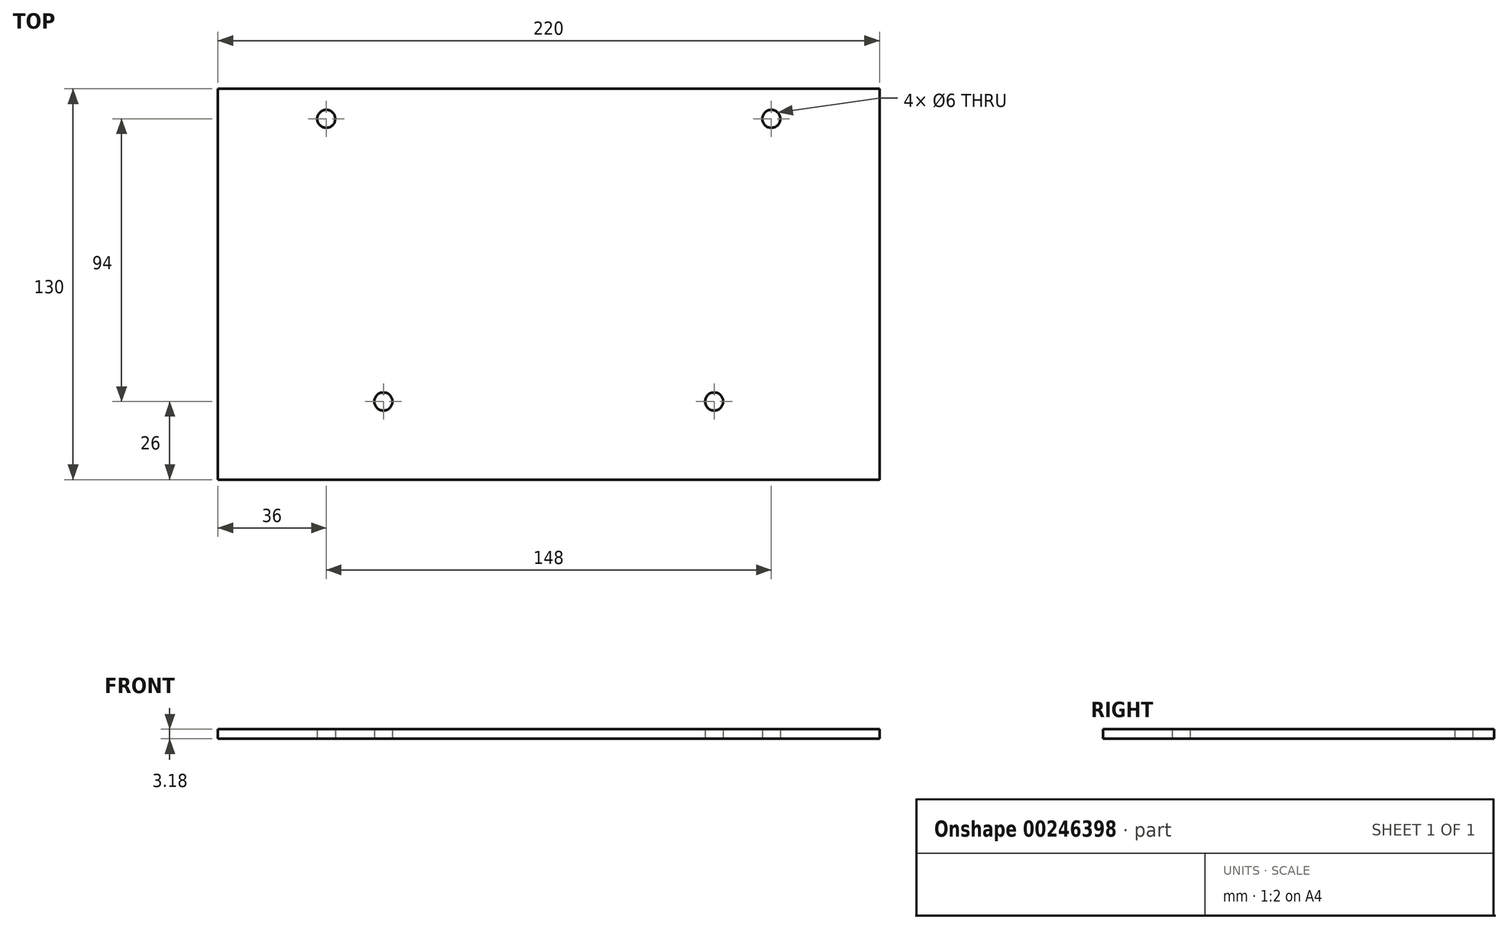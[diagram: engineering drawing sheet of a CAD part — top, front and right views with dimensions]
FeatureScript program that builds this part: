
annotation { "Feature Type Name" : "Feature", "Feature Type Description" : "" }
export const myFeature = defineFeature(function(context is Context, id is Id, definition is map)
    precondition{}
    {
        {
            var Q0;
            Q0=qCreatedBy(makeId("Top.planeOp"),FACE);
            var sketch = newSketch(context, id + "F0", { "sketchPlane" : qUnion([Q0])});
            skLineSegment(sketch, "E0.bottom", {"start": v(-110, 65) * mm, "end": v(110, 65) * mm});
            skLineSegment(sketch, "E0.top", {"start": v(-110, -65) * mm, "end": v(110, -65) * mm});
            skLineSegment(sketch, "E0.left", {"start": v(-110, 65) * mm, "end": v(-110, -65) * mm});
            skLineSegment(sketch, "E0.right", {"start": v(110, 65) * mm, "end": v(110, -65) * mm});
            skPoint(sketch, "E0.middle", {"position": v(0, 0) * mm});
            skLineSegment(sketch, "E1.0", {"start": v(-110, 55) * mm, "end": v(110, 55) * mm, "construction": true});
            skLineSegment(sketch, "E2", {"start": v(0, -65) * mm, "end": v(0, 65) * mm, "construction": true});
            skLineSegment(sketch, "E3.0", {"start": v(74, -65) * mm, "end": v(74, 65) * mm, "construction": true});
            skLineSegment(sketch, "E4.MirrorCS", {"start": v(-74, -65) * mm, "end": v(-74, 65) * mm, "construction": true});
            skCircle(sketch, "E5", {"center": v(-74, 55) * mm, "radius": 3 * mm});
            skCircle(sketch, "E6.MirrorC", {"center": v(74, 55) * mm, "radius": 3 * mm});
            skLineSegment(sketch, "E7.0", {"start": v(-110, -39) * mm, "end": v(110, -39) * mm, "construction": true});
            skLineSegment(sketch, "E8.0", {"start": v(55, -65) * mm, "end": v(55, 65) * mm, "construction": true});
            skCircle(sketch, "E9", {"center": v(55, -39) * mm, "radius": 3 * mm});
            skLineSegment(sketch, "E10.MirrorCS", {"start": v(-55, -65) * mm, "end": v(-55, 65) * mm, "construction": true});
            skCircle(sketch, "E11.MirrorC", {"center": v(-55, -39) * mm, "radius": 3 * mm});
            skSolve(sketch);
        }
        {
            var Q0;
            Q0=makeQuery(id+"F0.imprint","IMPRINT",FACE,{"disambiguationData":[TD([[makeQuery(id+"F0.imprint","IMPRINT",EDGE,{"derivedFrom":sQuery(id+"F0.wireOp",EDGE,"E0.bottom")}),-1.0]])]});
            extrude(context, id + "F1", {"entities" : qUnion([Q0]), "depth" : 3.17 * mm, "offsetDistance" : 25.4 * mm});
        }
    });
